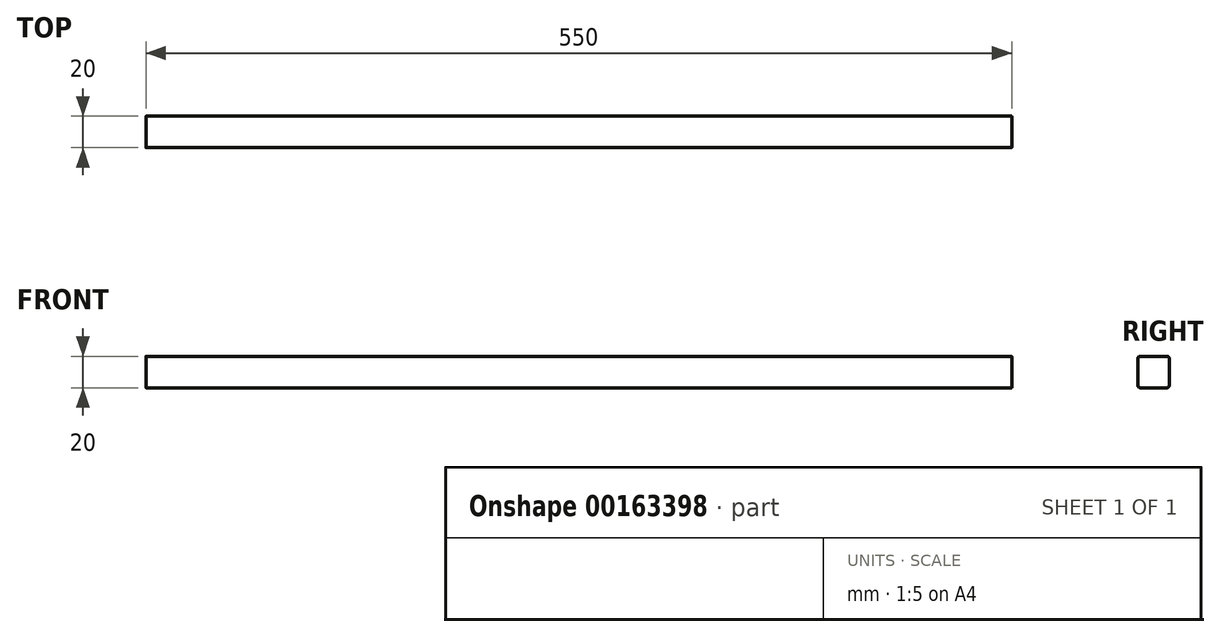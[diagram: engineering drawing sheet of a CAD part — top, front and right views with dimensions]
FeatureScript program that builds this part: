
annotation { "Feature Type Name" : "Feature", "Feature Type Description" : "" }
export const myFeature = defineFeature(function(context is Context, id is Id, definition is map)
    precondition{}
    {
        {
            var Q0;
            Q0=qCreatedBy(makeId("Right.planeOp"),FACE);
            var sketch = newSketch(context, id + "F0", { "sketchPlane" : qUnion([Q0])});
            skLineSegment(sketch, "E0.bottom", {"start": v(-8.5, 10) * mm, "end": v(8.5, 10) * mm});
            skLineSegment(sketch, "E0.top", {"start": v(-8.5, -10) * mm, "end": v(8.5, -10) * mm});
            skLineSegment(sketch, "E0.left", {"start": v(-10, 8.5) * mm, "end": v(-10, -8.5) * mm});
            skLineSegment(sketch, "E0.right", {"start": v(10, 8.5) * mm, "end": v(10, -8.5) * mm});
            skPoint(sketch, "E1.visualSharp", {"position": v(-10, 10) * mm});
            skArc(sketch, "E1.filletArc", {"start": v(-8.5, 10) * mm, "mid": v(-9.56, 9.56) * mm, "end": v(-10, 8.5) * mm});
            skPoint(sketch, "E2.visualSharp", {"position": v(10, 10) * mm});
            skArc(sketch, "E2.filletArc", {"start": v(10, 8.5) * mm, "mid": v(9.56, 9.56) * mm, "end": v(8.5, 10) * mm});
            skPoint(sketch, "E3.visualSharp", {"position": v(10, -10) * mm});
            skArc(sketch, "E3.filletArc", {"start": v(8.5, -10) * mm, "mid": v(9.56, -9.56) * mm, "end": v(10, -8.5) * mm});
            skPoint(sketch, "E4.visualSharp", {"position": v(-10, -10) * mm});
            skArc(sketch, "E4.filletArc", {"start": v(-10, -8.5) * mm, "mid": v(-9.56, -9.56) * mm, "end": v(-8.5, -10) * mm});
            skSolve(sketch);
        }
        {
            var Q0;
            Q0=makeQuery(id+"F0.imprint","IMPRINT",FACE,{"disambiguationData":[TD([[makeQuery(id+"F0.imprint","IMPRINT",EDGE,{"derivedFrom":sQuery(id+"F0.wireOp",EDGE,"E0.bottom")}),-1.0]])]});
            extrude(context, id + "F1", {"entities" : qUnion([Q0]), "endBound" : BoundingType.SYMMETRIC, "depth" : 550 * mm});
        }
    });
